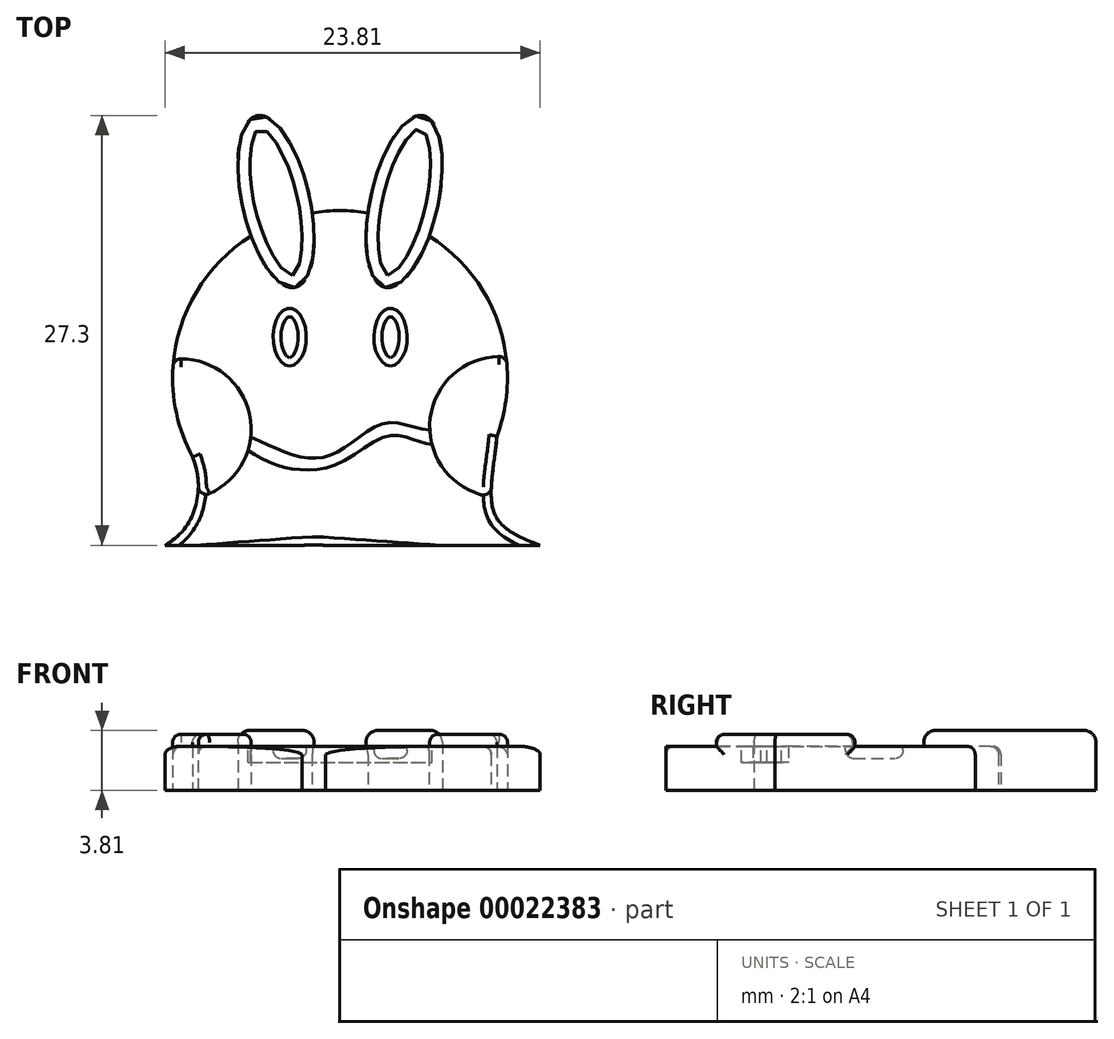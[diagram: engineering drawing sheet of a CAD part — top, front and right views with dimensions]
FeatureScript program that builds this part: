
annotation { "Feature Type Name" : "Feature", "Feature Type Description" : "" }
export const myFeature = defineFeature(function(context is Context, id is Id, definition is map)
    precondition{}
    {
        {
            var Q0;
            Q0=qCreatedBy(makeId("Top.planeOp"),FACE);
            var sketch = newSketch(context, id + "F0", { "sketchPlane" : qUnion([Q0])});
            skLineSegment(sketch, "E0.rect.bottom", {"start": v(12.7, 12.7) * mm, "end": v(-12.7, 12.7) * mm});
            skLineSegment(sketch, "E0.rect.top", {"start": v(12.7, -12.7) * mm, "end": v(-12.7, -12.7) * mm});
            skLineSegment(sketch, "E0.rect.left", {"start": v(12.7, 12.7) * mm, "end": v(12.7, -12.7) * mm});
            skLineSegment(sketch, "E0.rect.right", {"start": v(-12.7, 12.7) * mm, "end": v(-12.7, -12.7) * mm});
            skPoint(sketch, "E0.rect.middle", {"position": v(0, 0) * mm});
            skCircle(sketch, "E1", {"center": v(0, -2.07) * mm, "radius": 10.63 * mm});
            skFitSpline(sketch, "E2", {"points": [v(-9.37, -7.1) * mm, v(-9.24, -10.39) * mm, v(-11.1, -12.7) * mm], "startDerivative": vector(3.02, -7.5) * mm, "endDerivative": vector(-7.02, -4.32) * mm});
            skFitSpline(sketch, "E3", {"points": [v(9.96, -5.78) * mm, v(9.87, -10.83) * mm, v(12.7, -12.7) * mm], "startDerivative": vector(-0.96, -10.85) * mm, "endDerivative": vector(7.62, -3.03) * mm});
            skLineSegment(sketch, "E4", {"start": v(-11.1, -12.7) * mm, "end": v(12.7, -12.7) * mm});
            skFitSpline(sketch, "E5", {"points": [v(-11.1, -12.7) * mm, v(-11.52, -13.33) * mm, v(-8.29, -13.7) * mm, v(-2.42, -12.7) * mm, v(2.4, -13.25) * mm, v(7.8, -14.1) * mm, v(11.98, -13.97) * mm, v(12.93, -13.78) * mm, v(12.7, -12.7) * mm], "startDerivative": vector(-12.18, -10.76) * mm, "endDerivative": vector(-6.62, 17.28) * mm});
            skSolve(sketch);
        }
        {
            var Q0;
            {var subQ0=sQuery(id+"F0.wireOp",EDGE,"E5");var subQ1=sQuery(id+"F0.wireOp",EDGE,"E4");var subQ2=makeQuery(id+"F0.imprint","INTERSECT",VERTEX,{"disambiguationData":[OD(0.0)],"derivedFrom":[subQ1,subQ0]});Q0=makeQuery(id+"F0.imprint","IMPRINT",FACE,{"disambiguationData":[TD([[makeQuery(id+"F0.imprint","IMPRINT",EDGE,{"disambiguationData":[TD([[subQ2,1.0]])],"derivedFrom":subQ1}),-1.0]])]});}
            var Q1;
            {var subQ0=sQuery(id+"F0.wireOp",EDGE,"E5");var subQ1=sQuery(id+"F0.wireOp",EDGE,"E4");var subQ3=makeQuery(id+"F0.imprint","INTERSECT",VERTEX,{"disambiguationData":[OD(0.0)],"derivedFrom":[subQ1,subQ0]});Q1=makeQuery(id+"F0.imprint","IMPRINT",FACE,{"disambiguationData":[TD([[makeQuery(id+"F0.imprint","IMPRINT",EDGE,{"disambiguationData":[TD([[subQ3,-1.0]])],"derivedFrom":subQ1}),1.0]])]});}
            var Q2;
            {var subQ0=sQuery(id+"F0.wireOp",EDGE,"E5");var subQ1=sQuery(id+"F0.wireOp",EDGE,"E4");var subQ2=makeQuery(id+"F0.imprint","INTERSECT",VERTEX,{"disambiguationData":[OD(1.0)],"derivedFrom":[subQ1,subQ0]});Q2=makeQuery(id+"F0.imprint","IMPRINT",FACE,{"disambiguationData":[TD([[makeQuery(id+"F0.imprint","IMPRINT",EDGE,{"disambiguationData":[TD([[subQ2,-1.0]])],"derivedFrom":subQ1}),-1.0]])]});}
            var Q3;
            {var subQ3=sQuery(id+"F0.wireOp",EDGE,"E3");Q3=makeQuery(id+"F0.imprint","IMPRINT",FACE,{"disambiguationData":[TD([[makeQuery(id+"F0.imprint","IMPRINT",EDGE,{"derivedFrom":subQ3}),-1.0]])]});}
            var Q4;
            {var subQ6=sQuery(id+"F0.wireOp",EDGE,"E2");Q4=makeQuery(id+"F0.imprint","IMPRINT",FACE,{"disambiguationData":[TD([[makeQuery(id+"F0.imprint","IMPRINT",EDGE,{"derivedFrom":subQ6}),1.0]])]});}
            var Q5;
            {var subQ0=sQuery(id+"F0.wireOp",EDGE,"E1");var subQ2=makeQuery(id+"F0.imprint","INTERSECT",VERTEX,{"derivedFrom":[subQ0,sQuery(id+"F0.wireOp",EDGE,"E2")]});Q5=makeQuery(id+"F0.imprint","IMPRINT",FACE,{"disambiguationData":[TD([[makeQuery(id+"F0.imprint","IMPRINT",EDGE,{"disambiguationData":[TD([[subQ2,-1.0]])],"derivedFrom":subQ0}),1.0]])]});}
            extrude(context, id + "F1", {"entities" : qUnion([Q0, Q1, Q2, Q3, Q4, Q5]), "depth" : 2.8 * mm});
        }
        {
            var Q0;
            Q0=makeQuery(id+"F1.opExtrude","CAP_FACE",FACE,{"disambiguationData":[OSD([sQuery(id+"F0.wireOp",EDGE,"E1"),sQuery(id+"F0.wireOp",EDGE,"E2"),sQuery(id+"F0.wireOp",EDGE,"E3"),sQuery(id+"F0.wireOp",EDGE,"E4"),sQuery(id+"F0.wireOp",EDGE,"E5")])],"isStart":false});
            var sketch = newSketch(context, id + "F2", { "sketchPlane" : qUnion([Q0])});
            skCircle(sketch, "E6", {"center": v(-10.12, -5.33) * mm, "radius": 4.48 * mm});
            skCircle(sketch, "E7", {"center": v(10.17, -5.17) * mm, "radius": 4.48 * mm});
            skSolve(sketch);
        }
        {
            var Q0;
            {var subQ1=sQuery(id+"F2.wireOp",EDGE,"E6");var subQ3=makeQuery(id+"F1.opExtrude","CAP_EDGE",EDGE,{"disambiguationData":[OSD([sQuery(id+"F0.wireOp",EDGE,"E1")])],"isStart":false});var subQ5=makeQuery(id+"F2.imprint","INTERSECT",VERTEX,{"derivedFrom":[subQ3,subQ1]});Q0=makeQuery(id+"F2.imprint","IMPRINT",FACE,{"disambiguationData":[TD([[makeQuery(id+"F2.imprint","IMPRINT",EDGE,{"disambiguationData":[TD([[subQ5,1.0]])],"derivedFrom":subQ1}),1.0]])]});}
            var Q1;
            {var subQ1=sQuery(id+"F2.wireOp",EDGE,"E7");var subQ3=makeQuery(id+"F1.opExtrude","CAP_EDGE",EDGE,{"disambiguationData":[OSD([sQuery(id+"F0.wireOp",EDGE,"E1")])],"isStart":false});var subQ5=makeQuery(id+"F2.imprint","INTERSECT",VERTEX,{"derivedFrom":[subQ3,subQ1]});Q1=makeQuery(id+"F2.imprint","IMPRINT",FACE,{"disambiguationData":[TD([[makeQuery(id+"F2.imprint","IMPRINT",EDGE,{"disambiguationData":[TD([[subQ5,-1.0]])],"derivedFrom":subQ1}),1.0]])]});}
            extrude(context, id + "F3", {"entities" : qUnion([Q0, Q1]), "operationType" : NewBodyOperationType.ADD, "depth" : 0.76 * mm});
        }
        {
            var Q0;
            Q0=makeQuery(id+"F1.opExtrude","CAP_FACE",FACE,{"disambiguationData":[OSD([sQuery(id+"F0.wireOp",EDGE,"E1"),sQuery(id+"F0.wireOp",EDGE,"E2"),sQuery(id+"F0.wireOp",EDGE,"E3"),sQuery(id+"F0.wireOp",EDGE,"E4"),sQuery(id+"F0.wireOp",EDGE,"E5")])],"isStart":false});
            var sketch = newSketch(context, id + "F4", { "sketchPlane" : qUnion([Q0])});
            skFitSpline(sketch, "E8", {"points": [v(-5.67, -5.82) * mm, v(-2.4, -7.1) * mm, v(0, -6.68) * mm, v(2.9, -4.93) * mm, v(5.7, -5.37) * mm], "startDerivative": vector(12.64, -5.42) * mm, "endDerivative": vector(11.2, -0.54) * mm});
            skFitSpline(sketch, "E9", {"points": [v(-5.85, -6.68) * mm, v(-4.17, -7.55) * mm, v(-2.33, -7.9) * mm, v(0, -7.47) * mm, v(2.95, -5.77) * mm, v(4.6, -5.96) * mm, v(5.84, -6.3) * mm], "startDerivative": vector(9.26, -5.3) * mm, "endDerivative": vector(8.4, -1.49) * mm});
            skCircle(sketch, "E10", {"center": v(-10.12, -5.33) * mm, "radius": 4.48 * mm});
            skCircle(sketch, "E11", {"center": v(10.17, -5.17) * mm, "radius": 4.48 * mm});
            skSolve(sketch);
        }
        {
            var Q0;
            {var subQ2=sQuery(id+"F4.wireOp",EDGE,"E8");Q0=makeQuery(id+"F4.imprint","IMPRINT",FACE,{"disambiguationData":[TD([[makeQuery(id+"F4.imprint","IMPRINT",EDGE,{"derivedFrom":subQ2}),-1.0]])]});}
            extrude(context, id + "F5", {"entities" : qUnion([Q0]), "operationType" : NewBodyOperationType.REMOVE, "oppositeDirection" : true, "depth" : 1.02 * mm});
        }
        {
            var Q0;
            {var subQ0=sQuery(id+"F0.wireOp",EDGE,"E1");var subQ1=sQuery(id+"F0.wireOp",EDGE,"E2");var subQ2=sQuery(id+"F0.wireOp",EDGE,"E3");Q0=makeQuery(id+"F5.boolean.opBoolean","SPLIT",FACE,{"disambiguationData":[TD([makeQuery(id+"F1.opExtrude","SWEPT_FACE",FACE,{"disambiguationData":[OSD([subQ0])]})])],"derivedFrom":makeQuery(id+"F1.opExtrude","CAP_FACE",FACE,{"disambiguationData":[OSD([subQ0,subQ1,subQ2,sQuery(id+"F0.wireOp",EDGE,"E4"),sQuery(id+"F0.wireOp",EDGE,"E5")])],"isStart":false})});}
            var sketch = newSketch(context, id + "F6", { "sketchPlane" : qUnion([Q0])});
            skEllipse(sketch, "E12", {"center": v(-3.2, 0.53) * mm, "majorRadius": 1.83 * mm, "minorRadius": 1.06 * mm, "majorAxis": v(0, -1)});
            skLineSegment(sketch, "E13", {"start": v(0, 0) * mm, "end": v(0, 8.57) * mm});
            skEllipse(sketch, "E14.MirrorC", {"center": v(3.2, 0.53) * mm, "majorRadius": 1.83 * mm, "minorRadius": 1.06 * mm, "majorAxis": v(0, -1)});
            skSolve(sketch);
        }
        {
            var Q0;
            Q0 = qSketchRegion(id + "F6", true);
            extrude(context, id + "F7", {"entities" : qUnion([Q0]), "operationType" : NewBodyOperationType.REMOVE, "oppositeDirection" : true, "depth" : 0.76 * mm});
        }
        {
            var Q0;
            {var subQ0=sQuery(id+"F0.wireOp",EDGE,"E1");var subQ1=sQuery(id+"F0.wireOp",EDGE,"E2");var subQ2=sQuery(id+"F0.wireOp",EDGE,"E3");Q0=makeQuery(id+"F5.boolean.opBoolean","SPLIT",FACE,{"disambiguationData":[TD([makeQuery(id+"F1.opExtrude","SWEPT_FACE",FACE,{"disambiguationData":[OSD([subQ0])]})])],"derivedFrom":makeQuery(id+"F1.opExtrude","CAP_FACE",FACE,{"disambiguationData":[OSD([subQ0,subQ1,subQ2,sQuery(id+"F0.wireOp",EDGE,"E4"),sQuery(id+"F0.wireOp",EDGE,"E5")])],"isStart":false})});}
            var sketch = newSketch(context, id + "F8", { "sketchPlane" : qUnion([Q0])});
            skEllipse(sketch, "E15", {"center": v(-4.07, 9.14) * mm, "majorRadius": 5.58 * mm, "minorRadius": 2.14 * mm, "majorAxis": v(0.22, -0.98)});
            skLineSegment(sketch, "E16", {"start": v(0, 8.57) * mm, "end": v(0, 0) * mm});
            skEllipse(sketch, "E17.MirrorC", {"center": v(4.07, 9.14) * mm, "majorRadius": 5.58 * mm, "minorRadius": 2.14 * mm, "majorAxis": v(-0.22, -0.98)});
            skSolve(sketch);
        }
        {
            var Q0;
            Q0 = qSketchRegion(id + "F8", true);
            extrude(context, id + "F9", {"entities" : qUnion([Q0]), "operationType" : NewBodyOperationType.ADD, "depth" : 1.02 * mm, "hasSecondDirection" : true, "secondDirectionOppositeDirection" : true, "secondDirectionDepth" : 2.8 * mm});
        }
        {
            var Q0;
            Q0=makeQuery(id+"F3.opExtrude","CAP_EDGE",EDGE,{"disambiguationData":[OSD([sQuery(id+"F2.wireOp",EDGE,"E6")])],"isStart":false});
            var Q1;
            Q1=makeQuery(id+"F3.opExtrude","CAP_EDGE",EDGE,{"disambiguationData":[OSD([sQuery(id+"F2.wireOp",EDGE,"E7")])],"isStart":false});
            var Q2;
            {var subQ0=sQuery(id+"F0.wireOp",EDGE,"E5");var subQ1=sQuery(id+"F0.wireOp",EDGE,"E4");Q2=makeQuery(id+"F1.opExtrude","CAP_EDGE",EDGE,{"disambiguationData":[OSD([subQ0]),TDD([makeQuery(id+"F0.imprint","IMPRINT",EDGE,{"disambiguationData":[TD([[makeQuery(id+"F0.imprint","INTERSECT",VERTEX,{"disambiguationData":[OD(0.0)],"derivedFrom":[subQ1,subQ0]}),1.0]])],"derivedFrom":subQ0})])],"isStart":false});}
            var Q3;
            {var subQ0=sQuery(id+"F0.wireOp",EDGE,"E5");var subQ1=sQuery(id+"F0.wireOp",EDGE,"E4");Q3=makeQuery(id+"F1.opExtrude","CAP_EDGE",EDGE,{"disambiguationData":[OSD([subQ0]),TDD([makeQuery(id+"F0.imprint","IMPRINT",EDGE,{"disambiguationData":[TD([[makeQuery(id+"F0.imprint","INTERSECT",VERTEX,{"disambiguationData":[OD(1.0)],"derivedFrom":[subQ1,subQ0]}),-1.0]])],"derivedFrom":subQ0})])],"isStart":false});}
            var Q4;
            Q4=makeQuery(id+"F1.opExtrude","CAP_EDGE",EDGE,{"disambiguationData":[OSD([sQuery(id+"F0.wireOp",EDGE,"E4")])],"isStart":false});
            var Q5;
            Q5=makeQuery(id+"F1.opExtrude","CAP_EDGE",EDGE,{"disambiguationData":[OSD([sQuery(id+"F0.wireOp",EDGE,"E2")])],"isStart":false});
            var Q6;
            Q6=makeQuery(id+"F1.opExtrude","CAP_EDGE",EDGE,{"disambiguationData":[OSD([sQuery(id+"F0.wireOp",EDGE,"E3")])],"isStart":false});
            var Q7;
            Q7=makeQuery(id+"F7.boolean.opBoolean","COPY",FACE,{"derivedFrom":makeQuery(id+"F7.opExtrude","CAP_FACE",FACE,{"disambiguationData":[OSD([sQuery(id+"F6.wireOp",EDGE,"E12")])],"isStart":false})});
            var Q8;
            Q8=makeQuery(id+"F7.boolean.opBoolean","COPY",FACE,{"derivedFrom":makeQuery(id+"F7.opExtrude","CAP_FACE",FACE,{"disambiguationData":[OSD([sQuery(id+"F6.wireOp",EDGE,"E14.MirrorC")])],"isStart":false})});
            fillet(context, id + "F10", {"entities" : qUnion([Q0, Q1, Q2, Q3, Q4, Q5, Q6, Q7, Q8]), "radius" : 0.5 * mm, "tangentPropagation" : true, "allowEdgeOverflow" : false});
        }
        {
            var Q0;
            {var subQ0=sQuery(id+"F0.wireOp",EDGE,"E1");var subQ1=makeQuery(id+"F1.opExtrude","CAP_EDGE",EDGE,{"disambiguationData":[OSD([subQ0])],"isStart":false});Q0=makeQuery(id+"F3.opExtrude","CAP_EDGE",EDGE,{"disambiguationData":[OSD([subQ0]),TDD([makeQuery(id+"F2.imprint","IMPRINT",EDGE,{"disambiguationData":[TD([[makeQuery(id+"F2.imprint","INTERSECT",VERTEX,{"derivedFrom":[subQ1,makeQuery(id+"F1.opExtrude","CAP_EDGE",EDGE,{"disambiguationData":[OSD([sQuery(id+"F0.wireOp",EDGE,"E2")])],"isStart":false})]}),1.0]])],"derivedFrom":subQ1})])],"isStart":false});}
            var Q1;
            Q1=makeQuery(id+"F3.opExtrude","CAP_EDGE",EDGE,{"disambiguationData":[OSD([sQuery(id+"F0.wireOp",EDGE,"E2")])],"isStart":false});
            var Q2;
            {var subQ0=sQuery(id+"F0.wireOp",EDGE,"E1");var subQ1=makeQuery(id+"F1.opExtrude","CAP_EDGE",EDGE,{"disambiguationData":[OSD([subQ0])],"isStart":false});Q2=makeQuery(id+"F3.opExtrude","CAP_EDGE",EDGE,{"disambiguationData":[OSD([subQ0]),TDD([makeQuery(id+"F2.imprint","IMPRINT",EDGE,{"disambiguationData":[TD([[makeQuery(id+"F2.imprint","INTERSECT",VERTEX,{"derivedFrom":[subQ1,makeQuery(id+"F1.opExtrude","CAP_EDGE",EDGE,{"disambiguationData":[OSD([sQuery(id+"F0.wireOp",EDGE,"E3")])],"isStart":false})]}),-1.0]])],"derivedFrom":subQ1})])],"isStart":false});}
            var Q3;
            Q3=makeQuery(id+"F3.opExtrude","CAP_EDGE",EDGE,{"disambiguationData":[OSD([sQuery(id+"F0.wireOp",EDGE,"E3")])],"isStart":false});
            fillet(context, id + "F11", {"entities" : qUnion([Q0, Q1, Q2, Q3]), "radius" : 0.5 * mm, "tangentPropagation" : true, "allowEdgeOverflow" : false});
        }
        {
            var Q0;
            Q0=makeQuery(id+"F9.opExtrude","CAP_EDGE",EDGE,{"disambiguationData":[OSD([sQuery(id+"F8.wireOp",EDGE,"E15")])],"isStart":false});
            var Q1;
            Q1=makeQuery(id+"F9.opExtrude","CAP_EDGE",EDGE,{"disambiguationData":[OSD([sQuery(id+"F8.wireOp",EDGE,"E17.MirrorC")])],"isStart":false});
            fillet(context, id + "F12", {"entities" : qUnion([Q0, Q1]), "radius" : 0.76 * mm, "tangentPropagation" : true, "allowEdgeOverflow" : false});
        }
        {
            var Q0;
            {var subQ0=sQuery(id+"F0.wireOp",EDGE,"E1");var subQ1=makeQuery(id+"F1.opExtrude","CAP_EDGE",EDGE,{"disambiguationData":[OSD([subQ0])],"isStart":false});var subQ2=sQuery(id+"F2.wireOp",EDGE,"E6");var subQ3=sQuery(id+"F0.wireOp",EDGE,"E2");var subQ4=sQuery(id+"F0.wireOp",EDGE,"E3");Q0=makeQuery(id+"F9.boolean.opBoolean","SPLIT",EDGE,{"disambiguationData":[TD([makeQuery(id+"F1.opExtrude","SWEPT_FACE",FACE,{"disambiguationData":[OSD([subQ0])]}),makeQuery(id+"F1.opExtrude","CAP_FACE",FACE,{"disambiguationData":[OSD([subQ0,subQ3,subQ4,sQuery(id+"F0.wireOp",EDGE,"E4"),sQuery(id+"F0.wireOp",EDGE,"E5")])],"isStart":false}),makeQuery(id+"F3.opExtrude","SWEPT_FACE",FACE,{"disambiguationData":[OSD([subQ2])]}),makeQuery(id+"F3.opExtrude","SWEPT_FACE",FACE,{"disambiguationData":[OSD([subQ0]),TDD([makeQuery(id+"F2.imprint","IMPRINT",EDGE,{"disambiguationData":[TD([[makeQuery(id+"F2.imprint","INTERSECT",VERTEX,{"derivedFrom":[subQ1,makeQuery(id+"F1.opExtrude","CAP_EDGE",EDGE,{"disambiguationData":[OSD([subQ3])],"isStart":false})]}),1.0]])],"derivedFrom":subQ1})])]}),makeQuery(id+"F3.opExtrude","SWEPT_FACE",FACE,{"disambiguationData":[OSD([subQ0]),TDD([makeQuery(id+"F2.imprint","IMPRINT",EDGE,{"disambiguationData":[TD([[makeQuery(id+"F2.imprint","INTERSECT",VERTEX,{"derivedFrom":[subQ1,makeQuery(id+"F1.opExtrude","CAP_EDGE",EDGE,{"disambiguationData":[OSD([subQ4])],"isStart":false})]}),-1.0]])],"derivedFrom":subQ1})])]}),makeQuery(id+"F5.opExtrude","SWEPT_FACE",FACE,{"disambiguationData":[OSD([sQuery(id+"F4.wireOp",EDGE,"E10")])]}),makeQuery(id+"F9.opExtrude","SWEPT_FACE",FACE,{"disambiguationData":[OSD([sQuery(id+"F8.wireOp",EDGE,"E15")])]})])],"derivedFrom":subQ1});}
            var Q1;
            {var subQ0=sQuery(id+"F0.wireOp",EDGE,"E1");var subQ1=makeQuery(id+"F1.opExtrude","CAP_EDGE",EDGE,{"disambiguationData":[OSD([subQ0])],"isStart":false});var subQ2=sQuery(id+"F0.wireOp",EDGE,"E2");var subQ3=sQuery(id+"F0.wireOp",EDGE,"E3");Q1=makeQuery(id+"F9.boolean.opBoolean","SPLIT",EDGE,{"disambiguationData":[TD([makeQuery(id+"F1.opExtrude","SWEPT_FACE",FACE,{"disambiguationData":[OSD([subQ0])]}),makeQuery(id+"F1.opExtrude","CAP_FACE",FACE,{"disambiguationData":[OSD([subQ0,subQ2,subQ3,sQuery(id+"F0.wireOp",EDGE,"E4"),sQuery(id+"F0.wireOp",EDGE,"E5")])],"isStart":false}),makeQuery(id+"F3.opExtrude","SWEPT_FACE",FACE,{"disambiguationData":[OSD([subQ0]),TDD([makeQuery(id+"F2.imprint","IMPRINT",EDGE,{"disambiguationData":[TD([[makeQuery(id+"F2.imprint","INTERSECT",VERTEX,{"derivedFrom":[subQ1,makeQuery(id+"F1.opExtrude","CAP_EDGE",EDGE,{"disambiguationData":[OSD([subQ2])],"isStart":false})]}),1.0]])],"derivedFrom":subQ1})])]}),makeQuery(id+"F3.opExtrude","SWEPT_FACE",FACE,{"disambiguationData":[OSD([subQ0]),TDD([makeQuery(id+"F2.imprint","IMPRINT",EDGE,{"disambiguationData":[TD([[makeQuery(id+"F2.imprint","INTERSECT",VERTEX,{"derivedFrom":[subQ1,makeQuery(id+"F1.opExtrude","CAP_EDGE",EDGE,{"disambiguationData":[OSD([subQ3])],"isStart":false})]}),-1.0]])],"derivedFrom":subQ1})])]}),makeQuery(id+"F9.opExtrude","SWEPT_FACE",FACE,{"disambiguationData":[OSD([sQuery(id+"F8.wireOp",EDGE,"E15")])]}),makeQuery(id+"F9.opExtrude","SWEPT_FACE",FACE,{"disambiguationData":[OSD([sQuery(id+"F8.wireOp",EDGE,"E17.MirrorC")])]})])],"derivedFrom":subQ1});}
            var Q2;
            {var subQ0=sQuery(id+"F0.wireOp",EDGE,"E1");var subQ1=makeQuery(id+"F1.opExtrude","CAP_EDGE",EDGE,{"disambiguationData":[OSD([subQ0])],"isStart":false});var subQ2=sQuery(id+"F0.wireOp",EDGE,"E2");var subQ3=sQuery(id+"F2.wireOp",EDGE,"E7");var subQ4=sQuery(id+"F0.wireOp",EDGE,"E3");Q2=makeQuery(id+"F9.boolean.opBoolean","SPLIT",EDGE,{"disambiguationData":[TD([makeQuery(id+"F1.opExtrude","SWEPT_FACE",FACE,{"disambiguationData":[OSD([subQ0])]}),makeQuery(id+"F1.opExtrude","CAP_FACE",FACE,{"disambiguationData":[OSD([subQ0,subQ2,subQ4,sQuery(id+"F0.wireOp",EDGE,"E4"),sQuery(id+"F0.wireOp",EDGE,"E5")])],"isStart":false}),makeQuery(id+"F3.opExtrude","SWEPT_FACE",FACE,{"disambiguationData":[OSD([subQ3])]}),makeQuery(id+"F3.opExtrude","SWEPT_FACE",FACE,{"disambiguationData":[OSD([subQ0]),TDD([makeQuery(id+"F2.imprint","IMPRINT",EDGE,{"disambiguationData":[TD([[makeQuery(id+"F2.imprint","INTERSECT",VERTEX,{"derivedFrom":[subQ1,makeQuery(id+"F1.opExtrude","CAP_EDGE",EDGE,{"disambiguationData":[OSD([subQ2])],"isStart":false})]}),1.0]])],"derivedFrom":subQ1})])]}),makeQuery(id+"F3.opExtrude","SWEPT_FACE",FACE,{"disambiguationData":[OSD([subQ0]),TDD([makeQuery(id+"F2.imprint","IMPRINT",EDGE,{"disambiguationData":[TD([[makeQuery(id+"F2.imprint","INTERSECT",VERTEX,{"derivedFrom":[subQ1,makeQuery(id+"F1.opExtrude","CAP_EDGE",EDGE,{"disambiguationData":[OSD([subQ4])],"isStart":false})]}),-1.0]])],"derivedFrom":subQ1})])]}),makeQuery(id+"F5.opExtrude","SWEPT_FACE",FACE,{"disambiguationData":[OSD([sQuery(id+"F4.wireOp",EDGE,"E11")])]}),makeQuery(id+"F9.opExtrude","SWEPT_FACE",FACE,{"disambiguationData":[OSD([sQuery(id+"F8.wireOp",EDGE,"E17.MirrorC")])]})])],"derivedFrom":subQ1});}
            fillet(context, id + "F13", {"entities" : qUnion([Q0, Q1, Q2]), "radius" : 0.5 * mm, "tangentPropagation" : true, "allowEdgeOverflow" : false});
        }
    });
